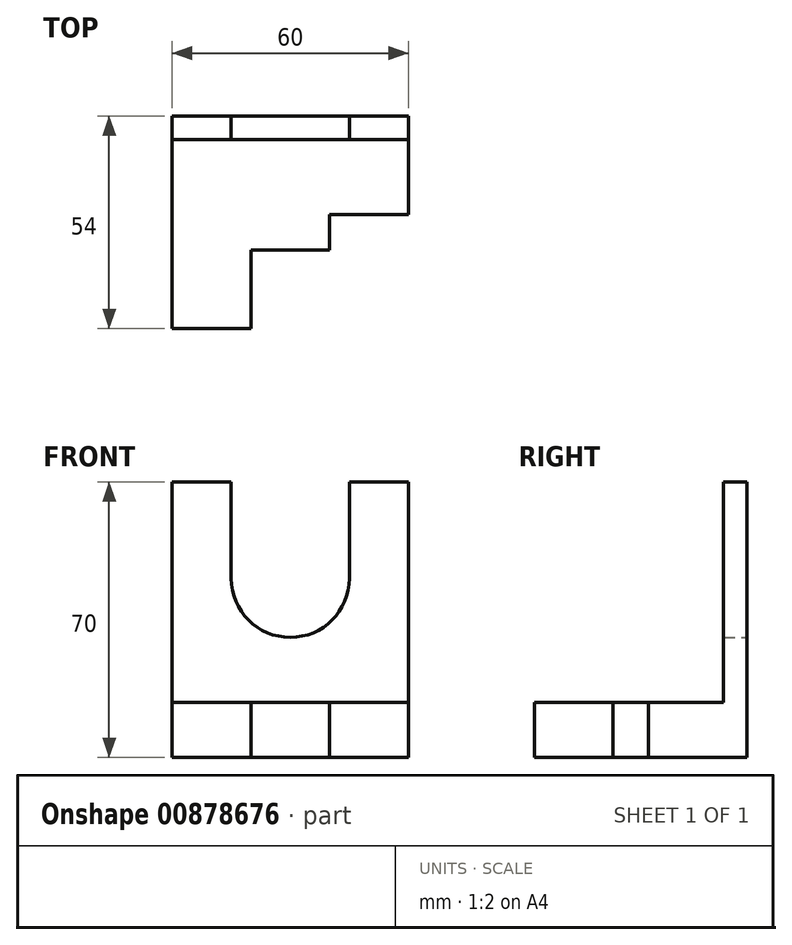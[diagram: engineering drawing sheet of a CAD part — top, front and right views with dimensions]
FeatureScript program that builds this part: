
annotation { "Feature Type Name" : "Feature", "Feature Type Description" : "" }
export const myFeature = defineFeature(function(context is Context, id is Id, definition is map)
    precondition{}
    {
        {
            var Q0;
            Q0=qCreatedBy(makeId("Front.planeOp"),FACE);
            var sketch = newSketch(context, id + "F0", { "sketchPlane" : qUnion([Q0])});
            skLineSegment(sketch, "E0.bottom", {"start": v(-30, -35) * mm, "end": v(30, -35) * mm});
            skLineSegment(sketch, "E0.top", {"start": v(-30, 35) * mm, "end": v(30, 35) * mm});
            skLineSegment(sketch, "E0.left", {"start": v(-30, -35) * mm, "end": v(-30, 35) * mm});
            skLineSegment(sketch, "E0.right", {"start": v(30, -35) * mm, "end": v(30, 35) * mm});
            skPoint(sketch, "E0.middle", {"position": v(0, 0) * mm});
            skLineSegment(sketch, "E1", {"start": v(-30, 35) * mm, "end": v(-15, 35) * mm});
            skLineSegment(sketch, "E2", {"start": v(-15, 35) * mm, "end": v(-15, 10) * mm});
            skLineSegment(sketch, "E3", {"start": v(30, 35) * mm, "end": v(15, 35) * mm});
            skLineSegment(sketch, "E4", {"start": v(15, 35) * mm, "end": v(15, 10) * mm});
            skArc(sketch, "E5", {"start": v(-15, 10.53) * mm, "mid": v(0, -4.47) * mm, "end": v(15, 10.53) * mm});
            skCircle(sketch, "E6", {"center": v(0, 10.53) * mm, "radius": 7.5 * mm});
            skLineSegment(sketch, "E7", {"start": v(30, -35) * mm, "end": v(30, -21) * mm});
            skLineSegment(sketch, "E8", {"start": v(30, -21) * mm, "end": v(10, -21) * mm});
            skLineSegment(sketch, "E9", {"start": v(10, -21) * mm, "end": v(10, -35) * mm});
            skLineSegment(sketch, "E10", {"start": v(10, -35) * mm, "end": v(-10, -35) * mm});
            skLineSegment(sketch, "E11", {"start": v(-10, -35) * mm, "end": v(-10, -21) * mm});
            skLineSegment(sketch, "E12", {"start": v(-10, -21) * mm, "end": v(10, -21) * mm});
            skLineSegment(sketch, "E13", {"start": v(-30, -21) * mm, "end": v(-10, -21) * mm});
            skSolve(sketch);
        }
        {
            var Q0;
            {var subQ0=sQuery(id+"F0.wireOp",EDGE,"E7");Q0=makeQuery(id+"F0.imprint","IMPRINT",FACE,{"disambiguationData":[TD([[makeQuery(id+"F0.imprint","IMPRINT",EDGE,{"derivedFrom":subQ0}),1.0]])]});}
            var Q1;
            {var subQ3=sQuery(id+"F0.wireOp",EDGE,"E11");Q1=makeQuery(id+"F0.imprint","IMPRINT",FACE,{"disambiguationData":[TD([[makeQuery(id+"F0.imprint","IMPRINT",EDGE,{"derivedFrom":subQ3}),1.0]])]});}
            extrude(context, id + "F1", {"entities" : qUnion([Q0, Q1]), "depth" : 54 * mm, "offsetDistance" : 25 * mm});
        }
        {
            var Q0;
            Q0=makeQuery(id+"F0.imprint","IMPRINT",FACE,{"disambiguationData":[TD([[makeQuery(id+"F0.imprint","IMPRINT",EDGE,{"derivedFrom":sQuery(id+"F0.wireOp",EDGE,"E9")}),-1.0]])]});
            extrude(context, id + "F2", {"entities" : qUnion([Q0]), "depth" : 34 * mm, "offsetDistance" : 25 * mm});
        }
        {
            var Q0;
            Q0=makeQuery(id+"F0.imprint","IMPRINT",FACE,{"disambiguationData":[TD([[makeQuery(id+"F0.imprint","IMPRINT",EDGE,{"derivedFrom":sQuery(id+"F0.wireOp",EDGE,"E0.right")}),1.0]])]});
            extrude(context, id + "F3", {"entities" : qUnion([Q0]), "depth" : 25 * mm, "offsetDistance" : 25 * mm});
        }
        {
            var Q0;
            {var subQ2=sQuery(id+"F0.wireOp",EDGE,"E0.top");Q0=makeQuery(id+"F0.imprint","IMPRINT",FACE,{"disambiguationData":[TD([[makeQuery(id+"F0.imprint","IMPRINT",EDGE,{"derivedFrom":subQ2}),-1.0]])]});}
            extrude(context, id + "F4", {"entities" : qUnion([Q0]), "operationType" : NewBodyOperationType.ADD, "depth" : 6 * mm, "offsetDistance" : 25 * mm});
        }
    });
